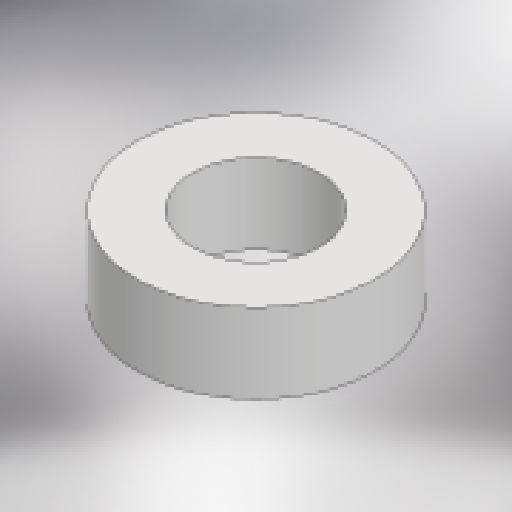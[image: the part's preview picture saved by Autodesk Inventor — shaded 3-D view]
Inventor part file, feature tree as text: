
AUTODESK INVENTOR PART (.ipt)
format: ipt  version: 2024 (Build 280153000, 153)  size: 135,168 bytes
history: native  units: in
note: dims shown in document units (in); Inventor stores cm internally (conversion verified against a paired STEP export)
features: extrude x1, sketch x1
ambient origin geometry x8: Origin, YZ Plane, XZ Plane, XY Plane, X Axis, Y Axis, Z Axis, Center Point
bodies: Solid1 (feature_tree)
feature tree (2):
  extrude  "Extrusion1"  Depth=0.125in
  sketch  "Sketch1"  dims[d0=0.375in d1=0.201in d2=0.125in d3=0.0in]
